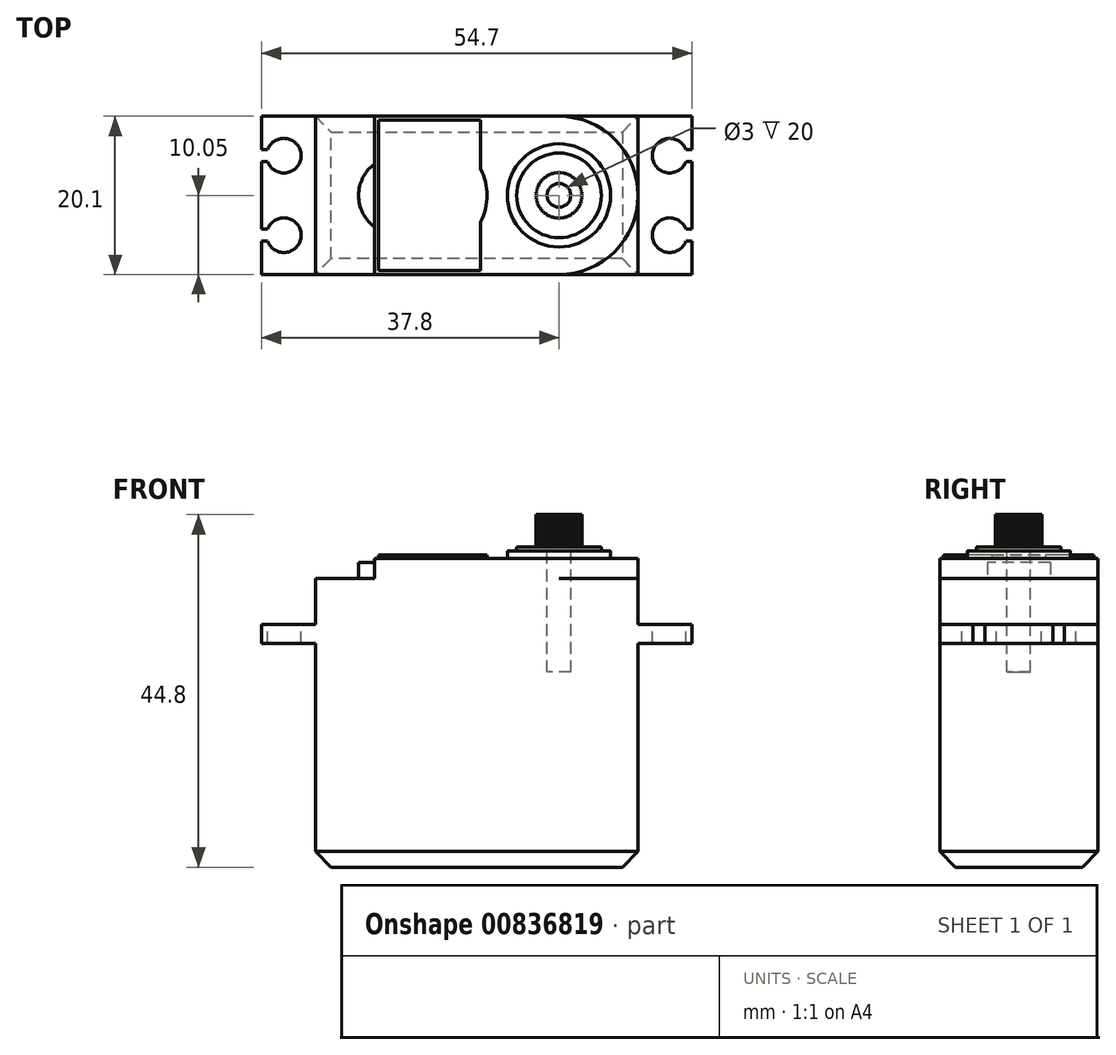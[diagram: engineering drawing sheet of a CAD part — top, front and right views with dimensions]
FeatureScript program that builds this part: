
annotation { "Feature Type Name" : "Feature", "Feature Type Description" : "" }
export const myFeature = defineFeature(function(context is Context, id is Id, definition is map)
    precondition{}
    {
        {
            var Q0;
            Q0=qCreatedBy(makeId("Top.planeOp"),FACE);
            var sketch = newSketch(context, id + "F0", { "sketchPlane" : qUnion([Q0])});
            skLineSegment(sketch, "E0.bottom", {"start": v(-30.95, 10.05) * mm, "end": v(10.05, 10.05) * mm});
            skLineSegment(sketch, "E0.top", {"start": v(-30.95, -10.05) * mm, "end": v(10.05, -10.05) * mm});
            skLineSegment(sketch, "E0.left", {"start": v(-30.95, 10.05) * mm, "end": v(-30.95, -10.05) * mm});
            skLineSegment(sketch, "E0.right", {"start": v(10.05, 10.05) * mm, "end": v(10.05, -10.05) * mm});
            skSolve(sketch);
        }
        {
            var Q0;
            Q0 = qSketchRegion(id + "F0", true);
            extrude(context, id + "F1", {"entities" : qUnion([Q0]), "depth" : 36.7 * mm, "offsetDistance" : 25 * mm});
        }
        {
            var Q0;
            Q0=makeQuery(id+"F1.opExtrude","CAP_FACE",FACE,{"disambiguationData":[OSD([sQuery(id+"F0.wireOp",EDGE,"E0.bottom"),sQuery(id+"F0.wireOp",EDGE,"E0.top"),sQuery(id+"F0.wireOp",EDGE,"E0.left"),sQuery(id+"F0.wireOp",EDGE,"E0.right")])],"isStart":false});
            var sketch = newSketch(context, id + "F2", { "sketchPlane" : qUnion([Q0])});
            skArc(sketch, "E1", {"start": v(0, -10.05) * mm, "mid": v(10.05, 0) * mm, "end": v(0, 10.05) * mm});
            skLineSegment(sketch, "E2", {"start": v(-23.45, 10.05) * mm, "end": v(-23.45, 4) * mm});
            skArc(sketch, "E3", {"start": v(-23.45, 4) * mm, "mid": v(-25.45, 0) * mm, "end": v(-23.45, -4) * mm});
            skLineSegment(sketch, "E4", {"start": v(-23.45, 10.05) * mm, "end": v(0, 10.05) * mm});
            skLineSegment(sketch, "E5", {"start": v(-23.45, -10.05) * mm, "end": v(0, -10.05) * mm});
            skLineSegment(sketch, "E6.trimOffspring", {"start": v(-23.45, -4) * mm, "end": v(-23.45, -10.05) * mm});
            skSolve(sketch);
        }
        {
            var Q0;
            Q0 = qSketchRegion(id + "F2", true);
            extrude(context, id + "F3", {"entities" : qUnion([Q0]), "operationType" : NewBodyOperationType.ADD, "depth" : 2.5 * mm, "offsetDistance" : 25 * mm});
        }
        {
            var Q0;
            Q0=makeQuery(id+"F3.opExtrude","CAP_FACE",FACE,{"disambiguationData":[OSD([sQuery(id+"F2.wireOp",EDGE,"E1"),sQuery(id+"F2.wireOp",EDGE,"E2"),sQuery(id+"F2.wireOp",EDGE,"E3"),sQuery(id+"F2.wireOp",EDGE,"E4"),sQuery(id+"F2.wireOp",EDGE,"E5"),sQuery(id+"F2.wireOp",EDGE,"E6.trimOffspring")])],"isStart":false});
            var sketch = newSketch(context, id + "F4", { "sketchPlane" : qUnion([Q0])});
            skLineSegment(sketch, "E7", {"start": v(-23.45, 4) * mm, "end": v(-23.45, -4) * mm});
            skSolve(sketch);
        }
        {
            var Q0;
            Q0=makeQuery(id+"F4.imprint","IMPRINT",FACE,{"disambiguationData":[TD([[makeQuery(id+"F4.imprint","IMPRINT",EDGE,{"derivedFrom":sQuery(id+"F4.wireOp",EDGE,"E7")}),-1.0]])]});
            extrude(context, id + "F5", {"entities" : qUnion([Q0]), "operationType" : NewBodyOperationType.REMOVE, "oppositeDirection" : true, "depth" : 0.5 * mm, "offsetDistance" : 25 * mm});
        }
        {
            var Q0;
            Q0=makeQuery(id+"F3.opExtrude","CAP_FACE",FACE,{"disambiguationData":[OSD([sQuery(id+"F2.wireOp",EDGE,"E1"),sQuery(id+"F2.wireOp",EDGE,"E2"),sQuery(id+"F2.wireOp",EDGE,"E3"),sQuery(id+"F2.wireOp",EDGE,"E4"),sQuery(id+"F2.wireOp",EDGE,"E5"),sQuery(id+"F2.wireOp",EDGE,"E6.trimOffspring")])],"isStart":false});
            var sketch = newSketch(context, id + "F6", { "sketchPlane" : qUnion([Q0])});
            skCircle(sketch, "E8", {"center": v(0, 0) * mm, "radius": 6.55 * mm});
            skSolve(sketch);
        }
        {
            var Q0;
            Q0=makeQuery(id+"F6.imprint","IMPRINT",FACE,{"disambiguationData":[TD([[makeQuery(id+"F6.imprint","IMPRINT",EDGE,{"derivedFrom":sQuery(id+"F6.wireOp",EDGE,"E8")}),1.0]])]});
            extrude(context, id + "F7", {"entities" : qUnion([Q0]), "operationType" : NewBodyOperationType.ADD, "depth" : 1 * mm, "offsetDistance" : 25 * mm});
        }
        {
            var Q0;
            Q0=makeQuery(id+"F7.opExtrude","CAP_FACE",FACE,{"disambiguationData":[OSD([sQuery(id+"F6.wireOp",EDGE,"E8")])],"isStart":false});
            var sketch = newSketch(context, id + "F8", { "sketchPlane" : qUnion([Q0])});
            skCircle(sketch, "E9", {"center": v(0, 0) * mm, "radius": 5.38 * mm});
            skSolve(sketch);
        }
        {
            var Q0;
            Q0=makeQuery(id+"F8.imprint","IMPRINT",FACE,{"disambiguationData":[TD([[makeQuery(id+"F8.imprint","IMPRINT",EDGE,{"derivedFrom":sQuery(id+"F8.wireOp",EDGE,"E9")}),1.0]])]});
            extrude(context, id + "F9", {"entities" : qUnion([Q0]), "operationType" : NewBodyOperationType.ADD, "depth" : 0.5 * mm, "offsetDistance" : 25 * mm});
        }
        {
            var Q0;
            Q0=makeQuery(id+"F9.opExtrude","CAP_FACE",FACE,{"disambiguationData":[OSD([sQuery(id+"F8.wireOp",EDGE,"E9")])],"isStart":false});
            var sketch = newSketch(context, id + "F10", { "sketchPlane" : qUnion([Q0])});
            skSolve(sketch);
        }
        {
            var Q0;
            Q0=makeQuery(id+"F10.imprint","IMPRINT",FACE,{"disambiguationData":[TD([[makeQuery(id+"F10.imprint","IMPRINT",EDGE,{"derivedFrom":makeQuery(id+"F9.opExtrude","CAP_EDGE",EDGE,{"disambiguationData":[OSD([sQuery(id+"F8.wireOp",EDGE,"E9")])],"isStart":false})}),1.0]])]});
            var sketch = newSketch(context, id + "F11", { "sketchPlane" : qUnion([Q0])});
            skCircle(sketch, "E10", {"center": v(0, 0) * mm, "radius": 2.95 * mm, "construction": true});
            skLineSegment(sketch, "E11", {"start": v(0, 0) * mm, "end": v(0, -2.95) * mm, "construction": true});
            skLineSegment(sketch, "E12", {"start": v(-0.51, -2.9) * mm, "end": v(0, 0) * mm, "construction": true});
            skLineSegment(sketch, "E13", {"start": v(-0.32, -3.65) * mm, "end": v(0, 0) * mm, "construction": true});
            skLineSegment(sketch, "E14", {"start": v(0, -2.95) * mm, "end": v(-0.25, -2.84) * mm});
            skLineSegment(sketch, "E15", {"start": v(-0.25, -2.84) * mm, "end": v(-0.51, -2.9) * mm});
            skLineSegment(sketch, "E16.1.0", {"start": v(0.25, -2.84) * mm, "end": v(0, -2.95) * mm});
            skLineSegment(sketch, "E16.1.1", {"start": v(0.51, -2.9) * mm, "end": v(0.25, -2.84) * mm});
            skLineSegment(sketch, "E16.2.0", {"start": v(0.74, -2.75) * mm, "end": v(0.51, -2.9) * mm});
            skLineSegment(sketch, "E16.2.1", {"start": v(1, -2.77) * mm, "end": v(0.74, -2.75) * mm});
            skLineSegment(sketch, "E16.3.0", {"start": v(1.2, -2.58) * mm, "end": v(1, -2.77) * mm});
            skLineSegment(sketch, "E16.3.1", {"start": v(1.47, -2.55) * mm, "end": v(1.2, -2.58) * mm});
            skLineSegment(sketch, "E16.4.0", {"start": v(1.63, -2.33) * mm, "end": v(1.48, -2.55) * mm});
            skLineSegment(sketch, "E16.4.1", {"start": v(1.9, -2.26) * mm, "end": v(1.63, -2.33) * mm});
            skLineSegment(sketch, "E16.5.0", {"start": v(2.02, -2.02) * mm, "end": v(1.9, -2.26) * mm});
            skLineSegment(sketch, "E16.5.1", {"start": v(2.26, -1.9) * mm, "end": v(2.02, -2.02) * mm});
            skLineSegment(sketch, "E16.6.0", {"start": v(2.33, -1.63) * mm, "end": v(2.26, -1.9) * mm});
            skLineSegment(sketch, "E16.6.1", {"start": v(2.55, -1.48) * mm, "end": v(2.33, -1.63) * mm});
            skLineSegment(sketch, "E16.7.0", {"start": v(2.58, -1.2) * mm, "end": v(2.55, -1.47) * mm});
            skLineSegment(sketch, "E16.7.1", {"start": v(2.77, -1) * mm, "end": v(2.58, -1.2) * mm});
            skLineSegment(sketch, "E16.8.0", {"start": v(2.75, -0.74) * mm, "end": v(2.77, -1) * mm});
            skLineSegment(sketch, "E16.8.1", {"start": v(2.9, -0.51) * mm, "end": v(2.75, -0.74) * mm});
            skLineSegment(sketch, "E16.9.0", {"start": v(2.84, -0.25) * mm, "end": v(2.9, -0.51) * mm});
            skLineSegment(sketch, "E16.9.1", {"start": v(2.95, 0) * mm, "end": v(2.84, -0.25) * mm});
            skLineSegment(sketch, "E16.10.0", {"start": v(2.84, 0.25) * mm, "end": v(2.95, 0) * mm});
            skLineSegment(sketch, "E16.10.1", {"start": v(2.9, 0.51) * mm, "end": v(2.84, 0.25) * mm});
            skLineSegment(sketch, "E16.11.0", {"start": v(2.75, 0.74) * mm, "end": v(2.9, 0.51) * mm});
            skLineSegment(sketch, "E16.11.1", {"start": v(2.77, 1) * mm, "end": v(2.75, 0.74) * mm});
            skLineSegment(sketch, "E16.12.0", {"start": v(2.58, 1.2) * mm, "end": v(2.77, 1) * mm});
            skLineSegment(sketch, "E16.12.1", {"start": v(2.55, 1.47) * mm, "end": v(2.58, 1.2) * mm});
            skLineSegment(sketch, "E16.13.0", {"start": v(2.33, 1.63) * mm, "end": v(2.55, 1.48) * mm});
            skLineSegment(sketch, "E16.13.1", {"start": v(2.26, 1.9) * mm, "end": v(2.33, 1.63) * mm});
            skLineSegment(sketch, "E16.14.0", {"start": v(2.02, 2.02) * mm, "end": v(2.26, 1.9) * mm});
            skLineSegment(sketch, "E16.14.1", {"start": v(1.9, 2.26) * mm, "end": v(2.02, 2.02) * mm});
            skLineSegment(sketch, "E16.15.0", {"start": v(1.63, 2.33) * mm, "end": v(1.9, 2.26) * mm});
            skLineSegment(sketch, "E16.15.1", {"start": v(1.48, 2.55) * mm, "end": v(1.63, 2.33) * mm});
            skLineSegment(sketch, "E16.16.0", {"start": v(1.2, 2.58) * mm, "end": v(1.47, 2.55) * mm});
            skLineSegment(sketch, "E16.16.1", {"start": v(1, 2.77) * mm, "end": v(1.2, 2.58) * mm});
            skLineSegment(sketch, "E16.17.0", {"start": v(0.74, 2.75) * mm, "end": v(1, 2.77) * mm});
            skLineSegment(sketch, "E16.17.1", {"start": v(0.51, 2.9) * mm, "end": v(0.74, 2.75) * mm});
            skLineSegment(sketch, "E16.18.0", {"start": v(0.25, 2.84) * mm, "end": v(0.51, 2.9) * mm});
            skLineSegment(sketch, "E16.18.1", {"start": v(0, 2.95) * mm, "end": v(0.25, 2.84) * mm});
            skLineSegment(sketch, "E16.19.0", {"start": v(-0.25, 2.84) * mm, "end": v(0, 2.95) * mm});
            skLineSegment(sketch, "E16.19.1", {"start": v(-0.51, 2.9) * mm, "end": v(-0.25, 2.84) * mm});
            skLineSegment(sketch, "E16.20.0", {"start": v(-0.74, 2.75) * mm, "end": v(-0.51, 2.9) * mm});
            skLineSegment(sketch, "E16.20.1", {"start": v(-1, 2.77) * mm, "end": v(-0.74, 2.75) * mm});
            skLineSegment(sketch, "E16.21.0", {"start": v(-1.2, 2.58) * mm, "end": v(-1, 2.77) * mm});
            skLineSegment(sketch, "E16.21.1", {"start": v(-1.48, 2.55) * mm, "end": v(-1.2, 2.58) * mm});
            skLineSegment(sketch, "E16.22.0", {"start": v(-1.63, 2.33) * mm, "end": v(-1.47, 2.55) * mm});
            skLineSegment(sketch, "E16.22.1", {"start": v(-1.9, 2.26) * mm, "end": v(-1.63, 2.33) * mm});
            skLineSegment(sketch, "E16.23.0", {"start": v(-2.02, 2.02) * mm, "end": v(-1.9, 2.26) * mm});
            skLineSegment(sketch, "E16.23.1", {"start": v(-2.26, 1.9) * mm, "end": v(-2.02, 2.02) * mm});
            skLineSegment(sketch, "E16.24.0", {"start": v(-2.33, 1.63) * mm, "end": v(-2.26, 1.9) * mm});
            skLineSegment(sketch, "E16.24.1", {"start": v(-2.55, 1.48) * mm, "end": v(-2.33, 1.63) * mm});
            skLineSegment(sketch, "E16.25.0", {"start": v(-2.58, 1.2) * mm, "end": v(-2.55, 1.47) * mm});
            skLineSegment(sketch, "E16.25.1", {"start": v(-2.77, 1) * mm, "end": v(-2.58, 1.2) * mm});
            skLineSegment(sketch, "E16.26.0", {"start": v(-2.75, 0.74) * mm, "end": v(-2.77, 1) * mm});
            skLineSegment(sketch, "E16.26.1", {"start": v(-2.9, 0.51) * mm, "end": v(-2.75, 0.74) * mm});
            skLineSegment(sketch, "E16.27.0", {"start": v(-2.84, 0.25) * mm, "end": v(-2.9, 0.51) * mm});
            skLineSegment(sketch, "E16.27.1", {"start": v(-2.95, 0) * mm, "end": v(-2.84, 0.25) * mm});
            skLineSegment(sketch, "E16.28.0", {"start": v(-2.84, -0.25) * mm, "end": v(-2.95, 0) * mm});
            skLineSegment(sketch, "E16.28.1", {"start": v(-2.9, -0.51) * mm, "end": v(-2.84, -0.25) * mm});
            skLineSegment(sketch, "E16.29.0", {"start": v(-2.75, -0.74) * mm, "end": v(-2.9, -0.51) * mm});
            skLineSegment(sketch, "E16.29.1", {"start": v(-2.77, -1) * mm, "end": v(-2.75, -0.74) * mm});
            skLineSegment(sketch, "E16.30.0", {"start": v(-2.58, -1.2) * mm, "end": v(-2.77, -1) * mm});
            skLineSegment(sketch, "E16.30.1", {"start": v(-2.55, -1.47) * mm, "end": v(-2.58, -1.2) * mm});
            skLineSegment(sketch, "E16.31.0", {"start": v(-2.33, -1.63) * mm, "end": v(-2.55, -1.48) * mm});
            skLineSegment(sketch, "E16.31.1", {"start": v(-2.26, -1.9) * mm, "end": v(-2.33, -1.63) * mm});
            skLineSegment(sketch, "E16.32.0", {"start": v(-2.02, -2.02) * mm, "end": v(-2.26, -1.9) * mm});
            skLineSegment(sketch, "E16.32.1", {"start": v(-1.9, -2.26) * mm, "end": v(-2.02, -2.02) * mm});
            skLineSegment(sketch, "E16.33.0", {"start": v(-1.63, -2.33) * mm, "end": v(-1.9, -2.26) * mm});
            skLineSegment(sketch, "E16.33.1", {"start": v(-1.47, -2.55) * mm, "end": v(-1.63, -2.33) * mm});
            skLineSegment(sketch, "E16.34.0", {"start": v(-1.2, -2.58) * mm, "end": v(-1.47, -2.55) * mm});
            skLineSegment(sketch, "E16.34.1", {"start": v(-1, -2.77) * mm, "end": v(-1.2, -2.58) * mm});
            skLineSegment(sketch, "E16.35.0", {"start": v(-0.74, -2.75) * mm, "end": v(-1, -2.77) * mm});
            skLineSegment(sketch, "E16.35.1", {"start": v(-0.51, -2.9) * mm, "end": v(-0.74, -2.75) * mm});
            skSolve(sketch);
        }
        {
            var Q0;
            Q0=makeQuery(id+"F11.imprint","IMPRINT",FACE,{"disambiguationData":[TD([[makeQuery(id+"F11.imprint","IMPRINT",EDGE,{"derivedFrom":sQuery(id+"F11.wireOp",EDGE,"E14")}),-1.0]])]});
            var Q1;
            Q1=sQuery(id+"F11.wireOp",EDGE,"E10");
            extrude(context, id + "F12", {"entities" : qUnion([Q0]), "operationType" : NewBodyOperationType.ADD, "surfaceEntities" : qUnion([Q1]), "depth" : 4.1 * mm, "offsetDistance" : 25 * mm});
        }
        {
            var Q0;
            Q0=makeQuery(id+"F1.opExtrude","CAP_EDGE",EDGE,{"disambiguationData":[OSD([sQuery(id+"F0.wireOp",EDGE,"E0.bottom")])],"isStart":true});
            var Q1;
            Q1=makeQuery(id+"F1.opExtrude","CAP_EDGE",EDGE,{"disambiguationData":[OSD([sQuery(id+"F0.wireOp",EDGE,"E0.right")])],"isStart":true});
            var Q2;
            Q2=makeQuery(id+"F1.opExtrude","CAP_EDGE",EDGE,{"disambiguationData":[OSD([sQuery(id+"F0.wireOp",EDGE,"E0.top")])],"isStart":true});
            var Q3;
            Q3=makeQuery(id+"F1.opExtrude","CAP_EDGE",EDGE,{"disambiguationData":[OSD([sQuery(id+"F0.wireOp",EDGE,"E0.left")])],"isStart":true});
            chamfer(context, id + "F13", {"entities" : qUnion([Q0, Q1, Q2, Q3]), "width" : 2 * mm, "tangentPropagation" : true});
        }
        {
            var Q0;
            {var subQ0=sQuery(id+"F0.wireOp",EDGE,"E0.left");var subQ1=sQuery(id+"F0.wireOp",EDGE,"E0.top");var subQ2=sQuery(id+"F0.wireOp",EDGE,"E0.bottom");Q0=makeQuery(id+"F3.boolean.opBoolean","SPLIT",FACE,{"disambiguationData":[TD([makeQuery(id+"F1.opExtrude","SWEPT_FACE",FACE,{"disambiguationData":[OSD([subQ2])]}),makeQuery(id+"F1.opExtrude","SWEPT_FACE",FACE,{"disambiguationData":[OSD([subQ1])]}),makeQuery(id+"F1.opExtrude","SWEPT_FACE",FACE,{"disambiguationData":[OSD([subQ0])]}),makeQuery(id+"F3.opExtrude","SWEPT_FACE",FACE,{"disambiguationData":[OSD([sQuery(id+"F2.wireOp",EDGE,"E2")])]}),makeQuery(id+"F3.opExtrude","SWEPT_FACE",FACE,{"disambiguationData":[OSD([sQuery(id+"F2.wireOp",EDGE,"E3")])]}),makeQuery(id+"F3.opExtrude","SWEPT_FACE",FACE,{"disambiguationData":[OSD([sQuery(id+"F2.wireOp",EDGE,"E4")])]}),makeQuery(id+"F3.opExtrude","SWEPT_FACE",FACE,{"disambiguationData":[OSD([sQuery(id+"F2.wireOp",EDGE,"E5")])]}),makeQuery(id+"F3.opExtrude","SWEPT_FACE",FACE,{"disambiguationData":[OSD([sQuery(id+"F2.wireOp",EDGE,"E6.trimOffspring")])]})])],"derivedFrom":makeQuery(id+"F1.opExtrude","CAP_FACE",FACE,{"disambiguationData":[OSD([subQ2,subQ1,subQ0,sQuery(id+"F0.wireOp",EDGE,"E0.right")])],"isStart":false})});}
            cPlane(context, id + "F14", {"entities" : qUnion([Q0]), "cplaneType" : CPlaneType.OFFSET, "offset" : 5.85 * mm, "oppositeDirection" : true, "width" : 150 * mm, "height" : 150 * mm});
        }
        {
            var Q0;
            Q0=qCreatedBy(id+"F14.planeOp",FACE);
            var sketch = newSketch(context, id + "F15", { "sketchPlane" : qUnion([Q0])});
            skLineSegment(sketch, "E17.0", {"start": v(-30.95, 10.05) * mm, "end": v(-30.95, -10.05) * mm, "construction": true});
            skLineSegment(sketch, "E18.0", {"start": v(10.05, 0) * mm, "end": v(10.05, -10.05) * mm});
            skLineSegment(sketch, "E19.0", {"start": v(10.05, 10.05) * mm, "end": v(10.05, 0) * mm});
            skLineSegment(sketch, "E20.bottom", {"start": v(-30.95, -10.05) * mm, "end": v(-37.8, -10.05) * mm});
            skLineSegment(sketch, "E20.top", {"start": v(-30.95, 10.05) * mm, "end": v(-37.8, 10.05) * mm});
            skLineSegment(sketch, "E20.left", {"start": v(-30.95, -10.05) * mm, "end": v(-30.95, 10.05) * mm});
            skLineSegment(sketch, "E20.right", {"start": v(-37.8, -10.05) * mm, "end": v(-37.8, 10.05) * mm});
            skPoint(sketch, "E21.oppositeSnap0", {"position": v(-34.38, 10.05) * mm});
            skLineSegment(sketch, "E21.bottom", {"start": v(10.05, -10.05) * mm, "end": v(16.9, -10.05) * mm});
            skLineSegment(sketch, "E21.top", {"start": v(10.05, 10.05) * mm, "end": v(16.9, 10.05) * mm});
            skLineSegment(sketch, "E21.left", {"start": v(10.05, -10.05) * mm, "end": v(10.05, 10.05) * mm});
            skLineSegment(sketch, "E21.right", {"start": v(16.9, -10.05) * mm, "end": v(16.9, 10.05) * mm});
            skSolve(sketch);
        }
        {
            var Q0;
            Q0 = qSketchRegion(id + "F15", true);
            extrude(context, id + "F16", {"entities" : qUnion([Q0]), "operationType" : NewBodyOperationType.ADD, "oppositeDirection" : true, "depth" : 2.4 * mm, "offsetDistance" : 25 * mm});
        }
        {
            var Q0;
            Q0=makeQuery(id+"F16.opExtrude","CAP_FACE",FACE,{"disambiguationData":[OSD([sQuery(id+"F15.wireOp",EDGE,"E20.bottom"),sQuery(id+"F15.wireOp",EDGE,"E20.top"),sQuery(id+"F15.wireOp",EDGE,"E20.left"),sQuery(id+"F15.wireOp",EDGE,"E20.right")])],"isStart":true});
            var sketch = newSketch(context, id + "F17", { "sketchPlane" : qUnion([Q0])});
            skArc(sketch, "E22", {"start": v(-37.02, 4.3) * mm, "mid": v(-32.75, 5.05) * mm, "end": v(-37.02, 5.8) * mm});
            skLineSegment(sketch, "E23.0", {"start": v(-30.95, 10.05) * mm, "end": v(-30.95, -10.05) * mm});
            skArc(sketch, "E24", {"start": v(16.12, 5.8) * mm, "mid": v(11.85, 5.05) * mm, "end": v(16.12, 4.3) * mm});
            skLineSegment(sketch, "E25.0", {"start": v(10.05, 10.05) * mm, "end": v(10.05, 0) * mm});
            skLineSegment(sketch, "E26.bottom", {"start": v(-38.72, 5.8) * mm, "end": v(-37.02, 5.8) * mm});
            skLineSegment(sketch, "E26.top", {"start": v(-38.72, 4.3) * mm, "end": v(-37.02, 4.3) * mm});
            skLineSegment(sketch, "E26.left", {"start": v(-38.72, 5.8) * mm, "end": v(-38.72, 4.3) * mm});
            skLineSegment(sketch, "E27.bottom", {"start": v(16.12, 5.8) * mm, "end": v(20.3, 5.8) * mm});
            skLineSegment(sketch, "E27.top", {"start": v(16.12, 4.3) * mm, "end": v(20.3, 4.3) * mm});
            skLineSegment(sketch, "E27.right", {"start": v(20.3, 5.8) * mm, "end": v(20.3, 4.3) * mm});
            skPoint(sketch, "E28.orphan", {"position": v(14.78, 4.3) * mm});
            skLineSegment(sketch, "E29.MirrorCS", {"start": v(-38.72, -5.8) * mm, "end": v(-37.02, -5.8) * mm});
            skLineSegment(sketch, "E30.MirrorCS", {"start": v(-38.72, -4.3) * mm, "end": v(-37.02, -4.3) * mm});
            skLineSegment(sketch, "E31.MirrorCS", {"start": v(-38.72, -5.8) * mm, "end": v(-38.72, -4.3) * mm});
            skArc(sketch, "E32.MirrorCS", {"start": v(-37.02, -4.3) * mm, "mid": v(-32.75, -5.05) * mm, "end": v(-37.02, -5.8) * mm});
            skLineSegment(sketch, "E33.MirrorCS", {"start": v(20.3, -5.8) * mm, "end": v(20.3, -4.3) * mm});
            skLineSegment(sketch, "E34.MirrorCS", {"start": v(16.12, -5.8) * mm, "end": v(20.3, -5.8) * mm});
            skLineSegment(sketch, "E35.MirrorCS", {"start": v(16.12, -4.3) * mm, "end": v(20.3, -4.3) * mm});
            skPoint(sketch, "E36.MirrorP", {"position": v(14.78, -4.3) * mm});
            skArc(sketch, "E37.MirrorCS", {"start": v(16.12, -5.8) * mm, "mid": v(11.85, -5.05) * mm, "end": v(16.12, -4.3) * mm});
            skCircle(sketch, "E38", {"center": v(0, 0) * mm, "radius": 14.93 * mm, "construction": true});
            skCircle(sketch, "E39", {"center": v(0, 0) * mm, "radius": 35.31 * mm, "construction": true});
            skSolve(sketch);
        }
        {
            var Q0;
            Q0 = qSketchRegion(id + "F17", true);
            extrude(context, id + "F18", {"entities" : qUnion([Q0]), "operationType" : NewBodyOperationType.REMOVE, "oppositeDirection" : true, "depth" : 25 * mm, "offsetDistance" : 25 * mm});
        }
        {
            var Q0;
            Q0=makeQuery(id+"F7.opExtrude","CAP_EDGE",EDGE,{"disambiguationData":[OSD([sQuery(id+"F6.wireOp",EDGE,"E8")])],"isStart":true});
            var Q1;
            Q1=makeQuery(id+"F7.opExtrude","CAP_EDGE",EDGE,{"disambiguationData":[OSD([sQuery(id+"F6.wireOp",EDGE,"E8")])],"isStart":false});
            var Q2;
            Q2=makeQuery(id+"F9.opExtrude","CAP_EDGE",EDGE,{"disambiguationData":[OSD([sQuery(id+"F8.wireOp",EDGE,"E9")])],"isStart":true});
            var Q3;
            Q3=makeQuery(id+"F9.opExtrude","CAP_EDGE",EDGE,{"disambiguationData":[OSD([sQuery(id+"F8.wireOp",EDGE,"E9")])],"isStart":false});
            fillet(context, id + "F19", {"entities" : qUnion([Q0, Q1, Q2, Q3]), "radius" : 0.1 * mm, "tangentPropagation" : true, "allowEdgeOverflow" : false});
        }
        {
            var Q0;
            Q0=makeQuery(id+"F12.opExtrude","CAP_FACE",FACE,{"disambiguationData":[OSD([sQuery(id+"F11.wireOp",EDGE,"E14"),sQuery(id+"F11.wireOp",EDGE,"E15"),sQuery(id+"F11.wireOp",EDGE,"E16.1.0"),sQuery(id+"F11.wireOp",EDGE,"E16.1.1"),sQuery(id+"F11.wireOp",EDGE,"E16.2.0"),sQuery(id+"F11.wireOp",EDGE,"E16.2.1"),sQuery(id+"F11.wireOp",EDGE,"E16.3.0"),sQuery(id+"F11.wireOp",EDGE,"E16.3.1"),sQuery(id+"F11.wireOp",EDGE,"E16.4.0"),sQuery(id+"F11.wireOp",EDGE,"E16.4.1"),sQuery(id+"F11.wireOp",EDGE,"E16.5.0"),sQuery(id+"F11.wireOp",EDGE,"E16.5.1"),sQuery(id+"F11.wireOp",EDGE,"E16.6.0"),sQuery(id+"F11.wireOp",EDGE,"E16.6.1"),sQuery(id+"F11.wireOp",EDGE,"E16.7.0"),sQuery(id+"F11.wireOp",EDGE,"E16.7.1"),sQuery(id+"F11.wireOp",EDGE,"E16.8.0"),sQuery(id+"F11.wireOp",EDGE,"E16.8.1"),sQuery(id+"F11.wireOp",EDGE,"E16.9.0"),sQuery(id+"F11.wireOp",EDGE,"E16.9.1"),sQuery(id+"F11.wireOp",EDGE,"E16.10.0"),sQuery(id+"F11.wireOp",EDGE,"E16.10.1"),sQuery(id+"F11.wireOp",EDGE,"E16.11.0"),sQuery(id+"F11.wireOp",EDGE,"E16.11.1"),sQuery(id+"F11.wireOp",EDGE,"E16.12.0"),sQuery(id+"F11.wireOp",EDGE,"E16.12.1"),sQuery(id+"F11.wireOp",EDGE,"E16.13.0"),sQuery(id+"F11.wireOp",EDGE,"E16.13.1"),sQuery(id+"F11.wireOp",EDGE,"E16.14.0"),sQuery(id+"F11.wireOp",EDGE,"E16.14.1"),sQuery(id+"F11.wireOp",EDGE,"E16.15.0"),sQuery(id+"F11.wireOp",EDGE,"E16.15.1"),sQuery(id+"F11.wireOp",EDGE,"E16.16.0"),sQuery(id+"F11.wireOp",EDGE,"E16.16.1"),sQuery(id+"F11.wireOp",EDGE,"E16.17.0"),sQuery(id+"F11.wireOp",EDGE,"E16.17.1"),sQuery(id+"F11.wireOp",EDGE,"E16.18.0"),sQuery(id+"F11.wireOp",EDGE,"E16.18.1"),sQuery(id+"F11.wireOp",EDGE,"E16.19.0"),sQuery(id+"F11.wireOp",EDGE,"E16.19.1"),sQuery(id+"F11.wireOp",EDGE,"E16.20.0"),sQuery(id+"F11.wireOp",EDGE,"E16.20.1"),sQuery(id+"F11.wireOp",EDGE,"E16.21.0"),sQuery(id+"F11.wireOp",EDGE,"E16.21.1"),sQuery(id+"F11.wireOp",EDGE,"E16.22.0"),sQuery(id+"F11.wireOp",EDGE,"E16.22.1"),sQuery(id+"F11.wireOp",EDGE,"E16.23.0"),sQuery(id+"F11.wireOp",EDGE,"E16.23.1"),sQuery(id+"F11.wireOp",EDGE,"E16.24.0"),sQuery(id+"F11.wireOp",EDGE,"E16.24.1"),sQuery(id+"F11.wireOp",EDGE,"E16.25.0"),sQuery(id+"F11.wireOp",EDGE,"E16.25.1"),sQuery(id+"F11.wireOp",EDGE,"E16.26.0"),sQuery(id+"F11.wireOp",EDGE,"E16.26.1"),sQuery(id+"F11.wireOp",EDGE,"E16.27.0"),sQuery(id+"F11.wireOp",EDGE,"E16.27.1"),sQuery(id+"F11.wireOp",EDGE,"E16.28.0"),sQuery(id+"F11.wireOp",EDGE,"E16.28.1"),sQuery(id+"F11.wireOp",EDGE,"E16.29.0"),sQuery(id+"F11.wireOp",EDGE,"E16.29.1"),sQuery(id+"F11.wireOp",EDGE,"E16.30.0"),sQuery(id+"F11.wireOp",EDGE,"E16.30.1"),sQuery(id+"F11.wireOp",EDGE,"E16.31.0"),sQuery(id+"F11.wireOp",EDGE,"E16.31.1"),sQuery(id+"F11.wireOp",EDGE,"E16.32.0"),sQuery(id+"F11.wireOp",EDGE,"E16.32.1"),sQuery(id+"F11.wireOp",EDGE,"E16.33.0"),sQuery(id+"F11.wireOp",EDGE,"E16.33.1"),sQuery(id+"F11.wireOp",EDGE,"E16.34.0"),sQuery(id+"F11.wireOp",EDGE,"E16.34.1"),sQuery(id+"F11.wireOp",EDGE,"E16.35.0"),sQuery(id+"F11.wireOp",EDGE,"E16.35.1")])],"isStart":false});
            var sketch = newSketch(context, id + "F20", { "sketchPlane" : qUnion([Q0])});
            skCircle(sketch, "E40", {"center": v(0, 0) * mm, "radius": 1.5 * mm});
            skSolve(sketch);
        }
        {
            var Q0;
            Q0=makeQuery(id+"F20.imprint","IMPRINT",FACE,{"disambiguationData":[TD([[makeQuery(id+"F20.imprint","IMPRINT",EDGE,{"derivedFrom":sQuery(id+"F20.wireOp",EDGE,"E40")}),1.0]])]});
            extrude(context, id + "F21", {"entities" : qUnion([Q0]), "operationType" : NewBodyOperationType.REMOVE, "oppositeDirection" : true, "depth" : 20 * mm, "offsetDistance" : 25 * mm});
        }
        {
            var Q0;
            Q0=makeQuery(id+"F3.opExtrude","CAP_FACE",FACE,{"disambiguationData":[OSD([sQuery(id+"F2.wireOp",EDGE,"E1"),sQuery(id+"F2.wireOp",EDGE,"E2"),sQuery(id+"F2.wireOp",EDGE,"E3"),sQuery(id+"F2.wireOp",EDGE,"E4"),sQuery(id+"F2.wireOp",EDGE,"E5"),sQuery(id+"F2.wireOp",EDGE,"E6.trimOffspring")])],"isStart":false});
            var sketch = newSketch(context, id + "F22", { "sketchPlane" : qUnion([Q0])});
            skLineSegment(sketch, "E41.bottom", {"start": v(-22.95, 9.55) * mm, "end": v(-9.96, 9.55) * mm});
            skLineSegment(sketch, "E41.top", {"start": v(-22.95, -9.55) * mm, "end": v(-9.96, -9.55) * mm});
            skLineSegment(sketch, "E41.left", {"start": v(-22.95, 9.55) * mm, "end": v(-22.95, -9.55) * mm});
            skLineSegment(sketch, "E41.right", {"start": v(-9.96, 9.55) * mm, "end": v(-9.96, 3.39) * mm});
            skLineSegment(sketch, "E42.0", {"start": v(-23.45, 10.05) * mm, "end": v(0, 10.05) * mm});
            skPoint(sketch, "E43.0", {"position": v(-11.72, -10.05) * mm});
            skCircle(sketch, "E44.0", {"center": v(0, 0) * mm, "radius": 6.65 * mm});
            skLineSegment(sketch, "E45.trimOffspring", {"start": v(-9.96, -3.39) * mm, "end": v(-9.96, -9.55) * mm});
            skArc(sketch, "E46.trimOffspring", {"start": v(-9.96, -3.39) * mm, "mid": v(-9.15, 0) * mm, "end": v(-9.96, 3.39) * mm});
            skPoint(sketch, "E47.orphan", {"position": v(-23.45, -10.05) * mm});
            skPoint(sketch, "E48.0.end.orphan", {"position": v(0, -10.05) * mm});
            skSolve(sketch);
        }
        {
            var Q0;
            Q0=makeQuery(id+"F22.imprint","IMPRINT",FACE,{"disambiguationData":[TD([[makeQuery(id+"F22.imprint","IMPRINT",EDGE,{"derivedFrom":sQuery(id+"F22.wireOp",EDGE,"E41.bottom")}),-1.0]])]});
            extrude(context, id + "F23", {"entities" : qUnion([Q0]), "operationType" : NewBodyOperationType.ADD, "depth" : 0.5 * mm, "offsetDistance" : 25 * mm});
        }
    });
